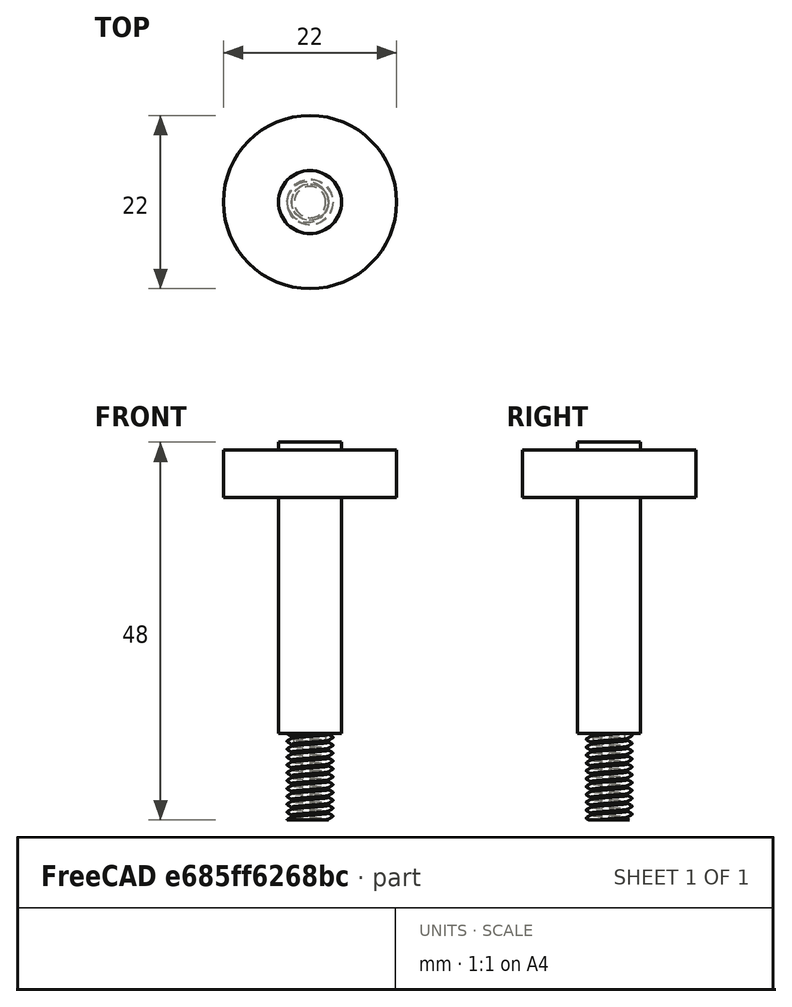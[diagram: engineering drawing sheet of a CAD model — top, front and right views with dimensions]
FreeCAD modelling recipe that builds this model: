
FCSTD DOCUMENT  (FreeCAD 0.20R29603 (Git))
Label: Estampo1Macho
License: All rights reserved
LicenseURL: http://en.wikipedia.org/wiki/All_rights_reserved
objects: TechDraw::DrawViewDimension×7, Sketcher::SketchObject×4, PartDesign::Pad×4, TechDraw::DrawViewPart×3, TechDraw::DrawViewBalloon×2, PartDesign::Body×1, TechDraw::DrawSVGTemplate×1, Part::FeaturePython×1, TechDraw::DrawViewAnnotation×1, TechDraw::DrawPage×1
note: 14 computed .brp shape members not serialized (recipe doc carries the construction recipe); baked Part::Feature solids carry a one-line shape summary decoded from their .brp

FEATURE [Sketcher::SketchObject] Sketch
  FullyConstrained = true
  MapMode = 5
  Support = -> [XY_Plane]
  sketch-geometry (1):
    g0: Circle CenterX=0 CenterY=0 CenterZ=0 NormalX=0 NormalY=0 NormalZ=1 AngleXU=0 Radius=4
  constraints (2):
    c: Coincident(g0,g-1)
    c: Diameter(g0) = 8
FEATURE [PartDesign::Pad] Pad  label="Haste"
  Direction = (0,0,1)
  Length = 30
  Length2 = 10
  Profile = -> Sketch
  ReferenceAxis = -> Sketch [N_Axis]
  Type = 0
FEATURE [Sketcher::SketchObject] Sketch001
  FullyConstrained = true
  MapMode = 5
  Placement = pos=(0,0,30) rot=(0,0,1;0rad)
  Support = -> [Pad]
  sketch-geometry (1):
    g0: Circle CenterX=0 CenterY=0 CenterZ=0 NormalX=0 NormalY=0 NormalZ=1 AngleXU=0 Radius=11
  constraints (2):
    c: Coincident(g0,g-1)
    c: Diameter(g0) = 22
FEATURE [PartDesign::Pad] Pad001  label="Base"
  BaseFeature = -> Pad
  Direction = (0,0,1)
  Length = 6
  Length2 = 10
  Profile = -> Sketch001
  ReferenceAxis = -> Sketch001 [N_Axis]
  Type = 0
FEATURE [Sketcher::SketchObject] Sketch002
  FullyConstrained = true
  MapMode = 5
  Placement = pos=(0,0,30) rot=(1,0,0;3.14159rad)
  Support = -> [Pad001]
  sketch-geometry (1):
    g0: Circle CenterX=0 CenterY=0 CenterZ=0 NormalX=0 NormalY=0 NormalZ=1 AngleXU=0 Radius=2
  constraints (2):
    c: Coincident(g0,g-1)
    c: Diameter(g0) = 4
FEATURE [PartDesign::Pad] Pad002  label="Rosca"
  BaseFeature = -> Pad001
  Direction = (0,0,-1)
  Length = 31
  Length2 = 10
  Profile = -> Sketch002
  ReferenceAxis = -> Sketch002 [N_Axis]
  Type = 0
FEATURE [Sketcher::SketchObject] Sketch003
  FullyConstrained = true
  MapMode = 5
  Placement = pos=(0,0,36) rot=(0,0,1;0rad)
  Support = -> [Pad002]
  sketch-geometry (1):
    g0: Circle CenterX=0 CenterY=0 CenterZ=0 NormalX=0 NormalY=0 NormalZ=1 AngleXU=0 Radius=4
  constraints (2):
    c: Coincident(g0,g-1)
    c: Diameter(g0) = 8
FEATURE [PartDesign::Pad] Pad003  label="Estampo"
  BaseFeature = -> Pad002
  Direction = (0,0,1)
  Length = 1
  Length2 = 10
  Profile = -> Sketch003
  ReferenceAxis = -> Sketch003 [N_Axis]
  Type = 0
FEATURE [PartDesign::Body] Body
  Group = -> [Sketch,Pad,Sketch001,Pad001,Sketch002,Pad002,Sketch003,Pad003]
  Origin = -> Origin
  Tip = -> Pad003
FEATURE [TechDraw::DrawSVGTemplate] Template
  EditableTexts = Designed_by_Name=Nilo; Drawing_number=-; FC-Date=31/03/2023; FC-SC=1:1; FC-SH=Sheet; FC-Title=Title; Subtitle=Estampo1 - Macho; Weight=?
  Height = 210
  Orientation = 1
  Width = 297
FEATURE [TechDraw::DrawViewPart] View001
  CoarseView = false
  Direction = (0,0,1)
  Focus = 100
  HardHidden = false
  IsoCount = 0
  IsoHidden = false
  IsoVisible = false
  LockPosition = false
  Perspective = false
  Rotation = 0
  ScaleType = 0
  SeamHidden = false
  SeamVisible = true
  SmoothHidden = false
  SmoothVisible = true
  Source = -> [Body]
  X = 96.5222
  XDirection = (1,0,0)
  Y = 168.156
FEATURE [Part::FeaturePython] ScrewTap  label="5.75x11-ScrewTap"  # Fasteners workbench fastener (typed FeaturePython)
  diameter = 33
  diameterCustom = 5.75
  invert = false
  leftHanded = false
  length = 11
  matchOuter = false
  offset = 0
  pitchCustom = 1
  thread = true
  type = 3
FEATURE [TechDraw::DrawViewPart] View
  CoarseView = false
  Direction = (0,-1,0)
  Focus = 100
  HardHidden = false
  IsoCount = 0
  IsoHidden = false
  IsoVisible = false
  LockPosition = false
  Perspective = false
  Rotation = 0
  ScaleType = 0
  SeamHidden = false
  SeamVisible = true
  SmoothHidden = false
  SmoothVisible = true
  Source = -> [Body,ScrewTap]
  X = 96.5474
  XDirection = (1,0,0)
  Y = 114.239
FEATURE [TechDraw::DrawViewPart] View002
  CoarseView = false
  Direction = (0.184,-0.886,0.425)
  Focus = 100
  HardHidden = false
  IsoCount = 0
  IsoHidden = false
  IsoVisible = false
  LockPosition = false
  Perspective = false
  Rotation = 0
  ScaleType = 0
  SeamHidden = false
  SeamVisible = true
  SmoothHidden = false
  SmoothVisible = true
  Source = -> [Body,ScrewTap,Origin,Pad,Pad001,Pad002,Pad003,Sketch002]
  X = 210.393
  XDirection = (0.846,0.363,0.391)
  Y = 144.28
FEATURE [TechDraw::DrawViewDimension] Dimension
  AngleOverride = false
  Arbitrary = false
  ArbitraryTolerances = false
  EqualTolerance = true
  ExtensionAngle = 0
  FormatSpec = %.2w
  FormatSpecOverTolerance = %+.2w
  FormatSpecUnderTolerance = %+.2w
  Inverted = false
  LineAngle = 0
  LockPosition = false
  MeasureType = 1
  OverTolerance = 0
  References2D = -> [View]
  Rotation = 0
  ScaleType = 0
  TheoreticalExact = false
  Type = 2
  UnderTolerance = 0
  X = 21.7031
  Y = 5.15447
FEATURE [TechDraw::DrawViewDimension] Dimension001
  AngleOverride = false
  Arbitrary = false
  ArbitraryTolerances = false
  EqualTolerance = true
  ExtensionAngle = 0
  FormatSpec = %.2w
  FormatSpecOverTolerance = %+.2w
  FormatSpecUnderTolerance = %+.2w
  Inverted = false
  LineAngle = 0
  LockPosition = false
  MeasureType = 1
  OverTolerance = 0
  References2D = -> [View]
  Rotation = 0
  ScaleType = 0
  TheoreticalExact = false
  Type = 2
  UnderTolerance = 0
  X = 27.7705
  Y = -13.7648
FEATURE [TechDraw::DrawViewDimension] Dimension004
  AngleOverride = false
  Arbitrary = false
  ArbitraryTolerances = false
  EqualTolerance = true
  ExtensionAngle = 0
  FormatSpec = R%.2w
  FormatSpecOverTolerance = %+.2w
  FormatSpecUnderTolerance = %+.2w
  Inverted = false
  LineAngle = 0
  LockPosition = false
  MeasureType = 1
  OverTolerance = 0
  References2D = -> [View001]
  Rotation = 0
  ScaleType = 0
  TheoreticalExact = false
  Type = 4
  UnderTolerance = 0
  X = 18.8629
  Y = 15.3698
FEATURE [TechDraw::DrawViewDimension] Dimension005
  AngleOverride = false
  Arbitrary = false
  ArbitraryTolerances = false
  EqualTolerance = true
  ExtensionAngle = 0
  FormatSpec = R%.2w
  FormatSpecOverTolerance = %+.2w
  FormatSpecUnderTolerance = %+.2w
  Inverted = false
  LineAngle = 0
  LockPosition = false
  MeasureType = 1
  OverTolerance = 0
  References2D = -> [View001]
  Rotation = 0
  ScaleType = 0
  TheoreticalExact = false
  Type = 4
  UnderTolerance = 0
  X = 20.493
  Y = -15.1369
FEATURE [TechDraw::DrawViewDimension] Dimension006
  AngleOverride = false
  Arbitrary = false
  ArbitraryTolerances = false
  EqualTolerance = true
  ExtensionAngle = 0
  FormatSpec = %.2w
  FormatSpecOverTolerance = %+.2w
  FormatSpecUnderTolerance = %+.2w
  Inverted = false
  LineAngle = 0
  LockPosition = false
  MeasureType = 1
  OverTolerance = 0
  References2D = -> [View]
  Rotation = 0
  ScaleType = 0
  TheoreticalExact = false
  Type = 2
  UnderTolerance = 0
  X = -25.5614
  Y = 25.2194
FEATURE [TechDraw::DrawViewDimension] Dimension008
  AngleOverride = false
  Arbitrary = false
  ArbitraryTolerances = false
  EqualTolerance = true
  ExtensionAngle = 0
  FormatSpec = %.2w
  FormatSpecOverTolerance = %+.2w
  FormatSpecUnderTolerance = %+.2w
  Inverted = false
  LineAngle = 0
  LockPosition = false
  MeasureType = 1
  OverTolerance = 0
  References2D = -> [View]
  Rotation = 0
  ScaleType = 0
  TheoreticalExact = false
  Type = 2
  UnderTolerance = 0
  X = -22.8577
  Y = -21.8049
FEATURE [TechDraw::DrawViewBalloon] Balloon
  BubbleShape = 0
  EndType = 0
  EndTypeScale = 1
  KinkLength = 5
  LockPosition = false
  OriginX = -12.7315
  OriginY = -11.4206
  Rotation = 0
  ScaleType = 0
  ShapeScale = 1
  SourceView = -> View002
  Text = 1
  TextWrapLen = -1
  X = -44.992
  Y = 14.0712
FEATURE [TechDraw::DrawViewAnnotation] Annotation
  Caption = Notas:
  Font = osifont
  LineSpace = 80
  LockPosition = false
  MaxWidth = -1
  Rotation = 0
  ScaleType = 0
  Text = 1 - Rosca M6 | 2 - Peça em aço AISI 304
  TextSize = 4
  TextStyle = 0
  X = 208.449
  Y = 89.6429
FEATURE [TechDraw::DrawViewDimension] Dimension009
  AngleOverride = false
  Arbitrary = false
  ArbitraryTolerances = false
  EqualTolerance = true
  ExtensionAngle = 0
  FormatSpec = ⌀%.2w
  FormatSpecOverTolerance = %+.2w
  FormatSpecUnderTolerance = %+.2w
  Inverted = false
  LineAngle = 0
  LockPosition = false
  MeasureType = 1
  OverTolerance = 0
  References2D = -> [View]
  Rotation = 0
  ScaleType = 0
  TheoreticalExact = false
  Type = 1
  UnderTolerance = 0
  X = -23.9535
  Y = 10.7894
FEATURE [TechDraw::DrawViewBalloon] Balloon001
  BubbleShape = 0
  EndType = 0
  EndTypeScale = 1
  KinkLength = 5
  LockPosition = false
  OriginX = -0.260113
  OriginY = -4.2826
  Rotation = 0
  ScaleType = 0
  ShapeScale = 1
  SourceView = -> View002
  Text = 2
  TextWrapLen = -1
  X = 33.8215
  Y = -2.95607
FEATURE [TechDraw::DrawPage] Page
  KeepUpdated = true
  NextBalloonIndex = 3
  ProjectionType = 0
  Template = -> Template
  Views = -> [View,View001,View002,Dimension,Dimension001,Dimension004,Dimension005,Dimension006,Dimension008,Balloon,Annotation,Dimension009,Balloon001]
